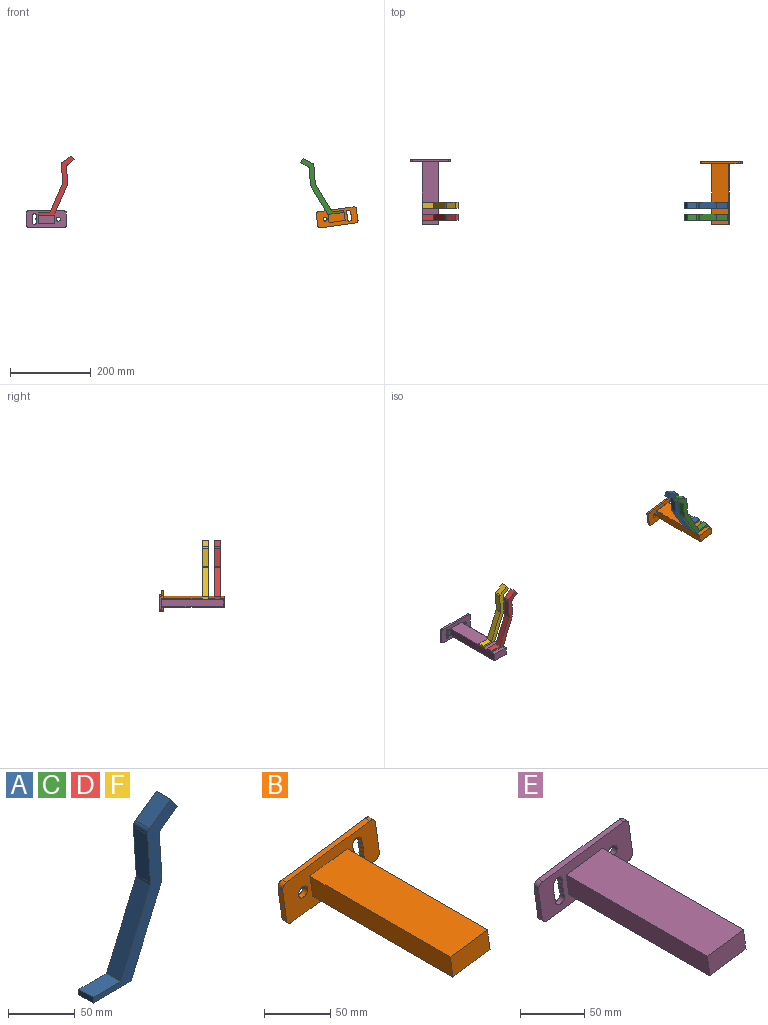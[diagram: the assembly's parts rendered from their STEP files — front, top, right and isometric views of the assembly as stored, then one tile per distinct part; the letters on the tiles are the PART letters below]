
ASSEMBLY  parts=6 mates=4
PART A: 18 faces, bbox 88.7x15x145.6 mm
  f0: plane 29.09x15mm, normal (0,0,1), area 436.3mm2, adj f1,f3,f4,f12
  f1: plane 15x5mm, normal (-1,0,0), area 75mm2, adj f0,f2,f3,f4
  f2: plane 40x15mm, normal (0,0,-1), area 600mm2, adj f1,f3,f4,f13
  f3: plane 145.64x88.73mm, normal (0,-1,0), area 2044.2mm2, adj f0,f1,f2,f5,f6,f7,f8,f9
  f4: plane 145.64x88.73mm, normal (0,1,0), area 2044.2mm2, adj f0,f1,f2,f5,f6,f7,f8,f9
  f5: cylinder r=5mm len=15mm, axis (0,1,0), area 75.9mm2, adj f3,f4,f6,f17
  f6: plane 16.7x15mm, normal (0.58,0,-0.81), area 308.7mm2, adj f3,f4,f5,f7
  f7: plane 15x9.74mm, normal (0.81,0,0.58), area 180mm2, adj f3,f4,f6,f8
  f8: plane 22.09x15.92mm, normal (-0.58,0,0.81), area 408.4mm2, adj f3,f4,f7,f9
  f9: cylinder r=5mm len=15mm, axis (0,1,0), area 75.9mm2, adj f3,f4,f8,f10
  f10: plane 45.92x15mm, normal (-1,0,-0.07), area 690.4mm2, adj f3,f4,f9,f11
  f11: cylinder r=5mm len=15mm, axis (0,1,0), area 35.5mm2, adj f3,f4,f10,f12
  f12: plane 72.1x31.1mm, normal (-0.92,0,0.4), area 1177.9mm2, adj f0,f3,f4,f11
  f13: plane 73.27x31.6mm, normal (0.92,0,-0.4), area 1197mm2, adj f2,f3,f4,f14
  f14: cylinder r=1.71mm len=15mm, axis (0,1,0), area 6.1mm2, adj f3,f4,f13,f15
  f15: plane 15x5.14mm, normal (0.99,0,-0.17), area 78.3mm2, adj f3,f4,f14,f16
  f16: cylinder r=1.71mm len=15mm, axis (0,1,0), area 6.1mm2, adj f3,f4,f15,f17
  f17: plane 40.29x15mm, normal (1,0,0.07), area 605.6mm2, adj f3,f4,f5,f16
PART B: 30 faces, bbox 103.3x155x52.2 mm
  f0: plane 103.3x52.23mm, normal (0,-1,0), area 2859mm2, adj f1,f2,f3,f4,f5,f6,f7,f8
  f1: cylinder r=5mm len=5mm, axis (0,1,0), area 23.4mm2, adj f0,f11,f14,f17
  f2: cylinder r=5mm len=5mm, axis (0,1,0), area 19.9mm2, adj f0,f11,f13,f18
  f3: plane 29.71x5mm, normal (0.99,0,0.14), area 150mm2, adj f0,f4,f10,f11
  f4: cylinder r=5mm len=5.65mm, axis (0,1,0), area 39.3mm2, adj f0,f3,f5,f11
  f5: plane 89.12x12.53mm, normal (-0.14,0,0.99), area 450mm2, adj f0,f4,f6,f11
  f6: cylinder r=5mm len=5.65mm, axis (0,1,0), area 39.3mm2, adj f0,f5,f7,f11
  f7: plane 29.71x5mm, normal (-0.99,0,-0.14), area 150mm2, adj f0,f6,f8,f11
  f8: cylinder r=5mm len=5.65mm, axis (0,1,0), area 39.3mm2, adj f0,f7,f9,f11
  f9: plane 89.12x12.53mm, normal (0.14,0,-0.99), area 450mm2, adj f0,f8,f10,f11
  f10: cylinder r=5mm len=5.65mm, axis (0,1,0), area 39.3mm2, adj f0,f3,f9,f11
  f11: plane 103.3x52.23mm, normal (0,1,0), area 3659mm2, adj f1,f2,f3,f4,f5,f6,f7,f8
  f12: cylinder r=5mm len=10mm, axis (0,1,0), area 157.1mm2, adj f0,f11
  f13: cylinder r=5mm len=5mm, axis (0,-1,0), area 19.9mm2, adj f0,f2,f11,f15
  f14: cylinder r=5mm len=5mm, axis (0,-1,0), area 23.4mm2, adj f0,f1,f11,f15
  f15: cylinder r=5mm len=10mm, axis (0,-1,0), area 100.1mm2, adj f0,f11,f13,f14
  f16: cylinder r=5mm len=10mm, axis (0,-1,0), area 100.1mm2, adj f0,f11,f17,f18
  f17: cylinder r=5mm len=5mm, axis (0,-1,0), area 23.4mm2, adj f0,f1,f11,f16
  f18: cylinder r=5mm len=5mm, axis (0,-1,0), area 19.9mm2, adj f0,f2,f11,f16
  f19: plane 42.39x25.37mm, normal (0,-1,0), area 800mm2, adj f20,f21,f22,f23
  f20: plane 150x19.81mm, normal (0.99,0,0.14), area 3000mm2, adj f0,f19,f21,f23
  f21: plane 150x39.61mm, normal (-0.14,0,0.99), area 6000mm2, adj f0,f19,f20,f22
  f22: plane 150x19.81mm, normal (-0.99,0,-0.14), area 3000mm2, adj f0,f19,f21,f23
  f23: plane 150x39.61mm, normal (0.14,0,-0.99), area 6000mm2, adj f0,f19,f20,f22
  f24: plane 148x15.84mm, normal (-0.99,0,-0.14), area 2368mm2, adj f25,f27,f28,f29
  f25: plane 148x35.65mm, normal (-0.14,0,0.99), area 5328mm2, adj f24,f26,f28,f29
  f26: plane 148x15.84mm, normal (0.99,0,0.14), area 2368mm2, adj f25,f27,f28,f29
  f27: plane 148x35.65mm, normal (0.14,0,-0.99), area 5328mm2, adj f24,f26,f28,f29
  f28: plane 37.88x20.85mm, normal (0,1,0), area 576mm2, adj f24,f25,f26,f27
  f29: plane 37.88x20.85mm, normal (0,-1,0), area 576mm2, adj f24,f25,f26,f27
PART C: same geometry as A
PART D: same geometry as A
PART E: 30 faces, bbox 103.3x160x52.2 mm
  f0: plane 103.3x52.23mm, normal (0,-1,0), area 2859mm2, adj f1,f2,f3,f4,f5,f6,f7,f8
  f1: cylinder r=5mm len=5mm, axis (0,1,0), area 23.4mm2, adj f0,f3,f15,f23
  f2: cylinder r=5mm len=5mm, axis (0,1,0), area 19.9mm2, adj f0,f4,f15,f23
  f3: cylinder r=5mm len=5mm, axis (0,1,0), area 23.4mm2, adj f0,f1,f6,f15
  f4: cylinder r=5mm len=5mm, axis (0,1,0), area 19.9mm2, adj f0,f2,f5,f15
  f5: cylinder r=5mm len=5mm, axis (0,1,0), area 19.9mm2, adj f0,f4,f15,f22
  f6: cylinder r=5mm len=5mm, axis (0,1,0), area 23.4mm2, adj f0,f3,f15,f22
  f7: plane 29.71x5mm, normal (0.99,0,0.14), area 150mm2, adj f0,f8,f14,f15
  f8: cylinder r=5mm len=5.65mm, axis (0,1,0), area 39.3mm2, adj f0,f7,f9,f15
  f9: plane 89.12x12.53mm, normal (-0.14,0,0.99), area 450mm2, adj f0,f8,f10,f15
  f10: cylinder r=5mm len=5.65mm, axis (0,1,0), area 39.3mm2, adj f0,f9,f11,f15
  f11: plane 29.71x5mm, normal (-0.99,0,-0.14), area 150mm2, adj f0,f10,f12,f15
  f12: cylinder r=5mm len=5.65mm, axis (0,1,0), area 39.3mm2, adj f0,f11,f13,f15
  f13: plane 89.12x12.53mm, normal (0.14,0,-0.99), area 450mm2, adj f0,f12,f14,f15
  f14: cylinder r=5mm len=5.65mm, axis (0,1,0), area 39.3mm2, adj f0,f7,f13,f15
  f15: plane 103.3x52.23mm, normal (0,1,0), area 3659mm2, adj f1,f2,f3,f4,f5,f6,f7,f8
  f16: cylinder r=5mm len=10mm, axis (0,1,0), area 157.1mm2, adj f0,f15
  f17: plane 42.39x25.37mm, normal (0,-1,0), area 800mm2, adj f18,f19,f20,f21
  f18: plane 155x19.81mm, normal (-0.99,0,-0.14), area 3100mm2, adj f0,f17,f19,f21
  f19: plane 155x39.61mm, normal (0.14,0,-0.99), area 6200mm2, adj f0,f17,f18,f20
  f20: plane 155x19.81mm, normal (0.99,0,0.14), area 3100mm2, adj f0,f17,f19,f21
  f21: plane 155x39.61mm, normal (-0.14,0,0.99), area 6200mm2, adj f0,f17,f18,f20
  f22: cylinder r=5mm len=10mm, axis (0,1,0), area 100.1mm2, adj f0,f5,f6,f15
  f23: cylinder r=5mm len=10mm, axis (0,1,0), area 100.1mm2, adj f0,f1,f2,f15
  f24: plane 153x15.84mm, normal (0.99,0,0.14), area 2448mm2, adj f25,f27,f28,f29
  f25: plane 153x35.65mm, normal (0.14,0,-0.99), area 5508mm2, adj f24,f26,f28,f29
  f26: plane 153x15.84mm, normal (-0.99,0,-0.14), area 2448mm2, adj f25,f27,f28,f29
  f27: plane 153x35.65mm, normal (-0.14,0,0.99), area 5508mm2, adj f24,f26,f28,f29
  f28: plane 37.88x20.85mm, normal (0,1,0), area 576mm2, adj f24,f25,f26,f27
  f29: plane 37.88x20.85mm, normal (0,-1,0), area 576mm2, adj f24,f25,f26,f27
PART F: same geometry as A
PLACE A rot(axis=(0.07,0,-1),180deg) t=(252.12,-150,147.57)mm
PLACE B rot(axis=(0,-1,0.01),0deg) t=(186.52,-35,-80.69)mm
PLACE C rot(axis=(0.07,0,-1),180deg) t=(252.12,-180,147.57)mm
PLACE D t=(-727.83,-165,125.21)mm
PLACE E rot(axis=(0,1,0),8deg) t=(-533.35,-30,15.67)mm
PLACE F t=(-727.83,-135,125.21)mm
MATE fastened C.f2 <-> B.f21  axis (0.14,0,-0.99) through (146.82,-180,41.68)mm
MATE fastened A.f2 <-> B.f21  axis (0.14,0,-0.99) through (146.82,-150,41.68)mm
MATE fastened F.f2 <-> E.f21  axis (0,0,-1) through (-608.82,-150,35)mm
MATE fastened D.f2 <-> E.f21  axis (0,0,-1) through (-608.82,-180,35)mm
